# Revit family: БПО_RV17_LOD400 (07.12.2023)
name_source: partatom
category: Электрооборудование
revit_build: Autodesk Revit 2017 (Build: 20170118_1100(x64)
units: mm (PartAtom-declared; Revit-internal decimal feet)

## family parameters
Всегда вертикально = Нет
Конфигурация панели = Два столбца, слева направо
На основе рабочей плоскости = Да
Общий = Нет
При загрузке вырезать с полостями = Нет
Размер круглого соединителя = Использовать диаметр
Тип детали = Щит
Точка расчета площади = Нет

## types (1)
- БПО
    ADSK_URL страницы изделия = https://stilsoft.ru
    ADSK_Единица измерения = шт.
    ADSK_Завод-изготовитель = ООО «Основа Безопасности»
    ADSK_Количество = 1
    ADSK_Марка = СТАЕ.426479.014
    ADSK_Масса = 1
    ADSK_Наименование = Блок БПО
    ADSK_Размер_Высота = 194 мм
    ADSK_Размер_Глубина = 80 мм
    ADSK_Размер_Длина = 292 мм
    d_короба = 20 мм
    Вариант исполнения в составе контроллера STS-504 = уличное
    Диапазон рабочих температур, °С = от –40 до +50
    Клеммы, для подключения дополнительного питания с сечением S=16 мм2 = 2
    Клеммы, для подключения оборудования с сечением S=0,5-4 мм2 = 14
    Отметка по умолчанию = 1219 мм
